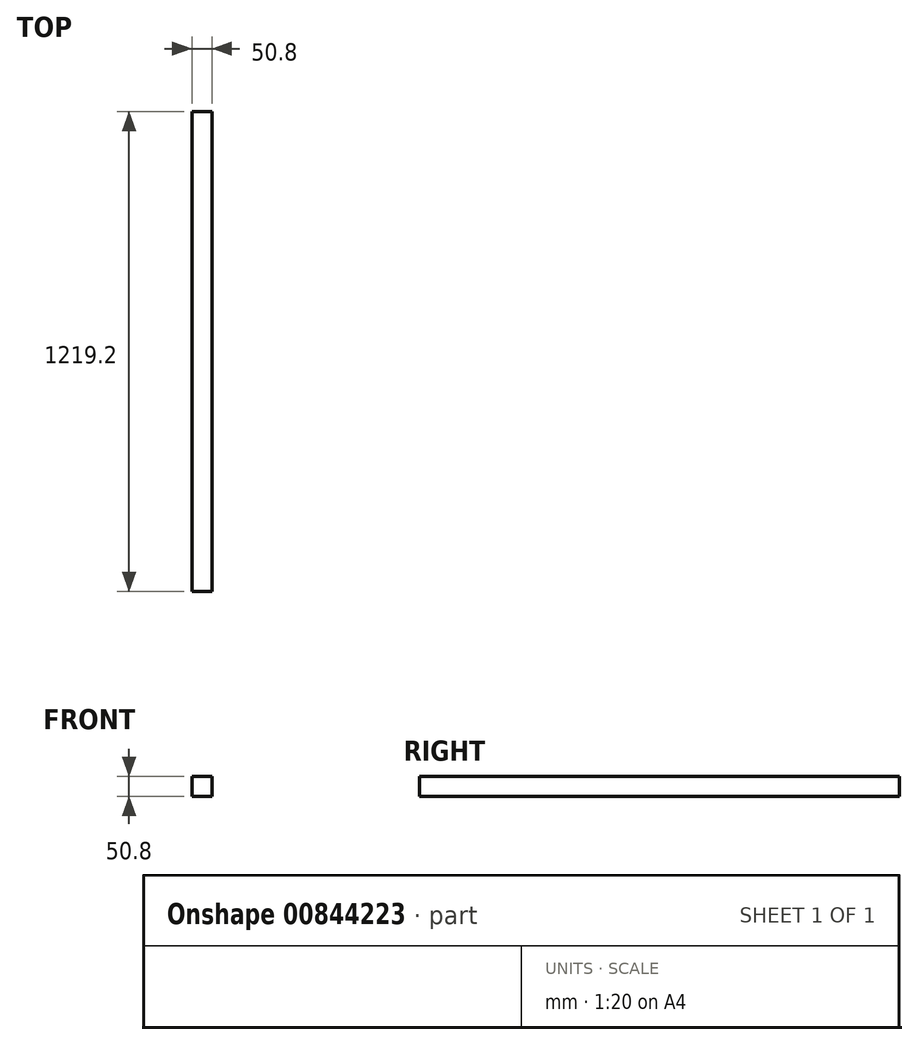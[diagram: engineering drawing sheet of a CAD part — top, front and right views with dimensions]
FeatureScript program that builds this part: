
annotation { "Feature Type Name" : "Feature", "Feature Type Description" : "" }
export const myFeature = defineFeature(function(context is Context, id is Id, definition is map)
    precondition{}
    {
        {
            var Q0;
            Q0=qCreatedBy(makeId("Front.planeOp"),FACE);
            var sketch = newSketch(context, id + "F0", { "sketchPlane" : qUnion([Q0])});
            skLineSegment(sketch, "E0.bottom", {"start": v(25.4, 25.4) * mm, "end": v(-25.4, 25.4) * mm});
            skLineSegment(sketch, "E0.top", {"start": v(25.4, -25.4) * mm, "end": v(-25.4, -25.4) * mm});
            skLineSegment(sketch, "E0.left", {"start": v(25.4, 25.4) * mm, "end": v(25.4, -25.4) * mm});
            skLineSegment(sketch, "E0.right", {"start": v(-25.4, 25.4) * mm, "end": v(-25.4, -25.4) * mm});
            skPoint(sketch, "E0.middle", {"position": v(0, 0) * mm});
            skSolve(sketch);
        }
        {
            var Q0;
            Q0 = qSketchRegion(id + "F0", true);
            extrude(context, id + "F1", {"entities" : qUnion([Q0]), "depth" : 1219.2 * mm, "offsetDistance" : 25.4 * mm});
        }
    });
